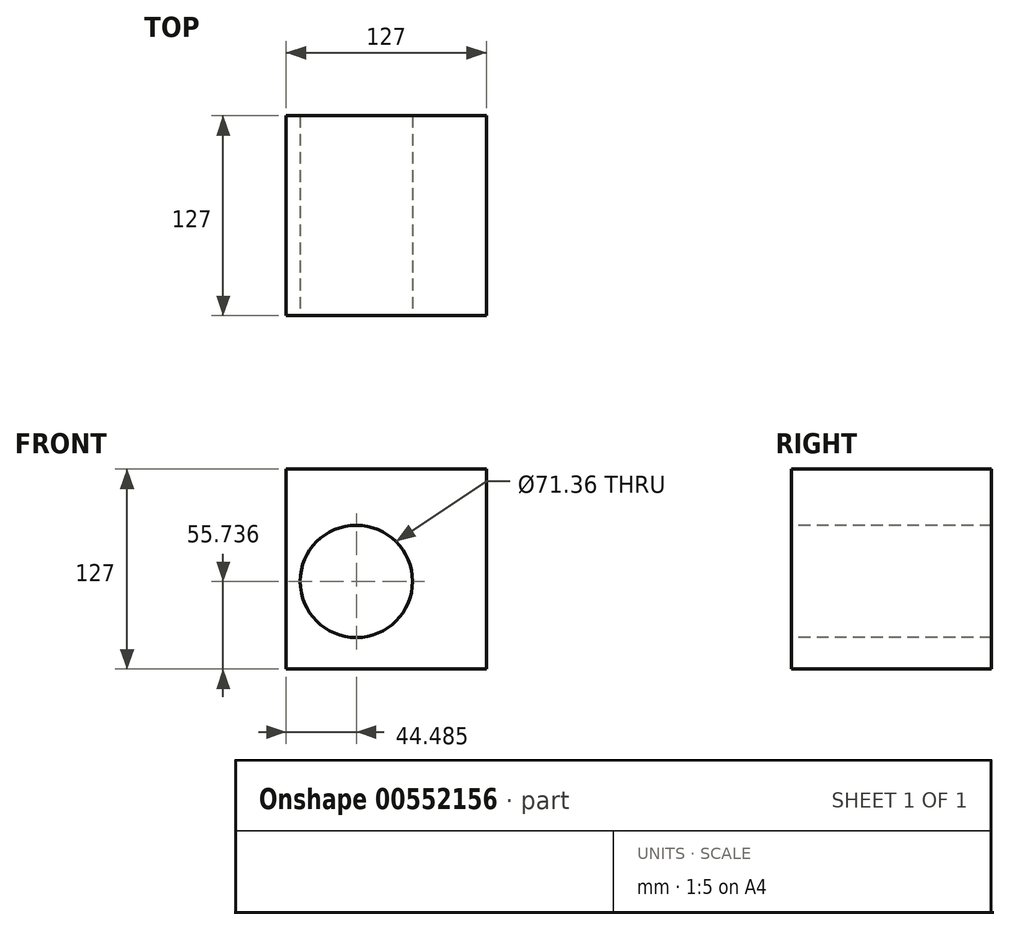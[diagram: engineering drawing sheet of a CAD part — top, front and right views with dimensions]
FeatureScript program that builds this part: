
annotation { "Feature Type Name" : "Feature", "Feature Type Description" : "" }
export const myFeature = defineFeature(function(context is Context, id is Id, definition is map)
    precondition{}
    {
        {
            var Q0;
            Q0=qCreatedBy(makeId("Front.planeOp"),FACE);
            var sketch = newSketch(context, id + "F0", { "sketchPlane" : qUnion([Q0])});
            skLineSegment(sketch, "E0.bottom", {"start": v(-65.6, 78.72) * mm, "end": v(61.4, 78.72) * mm});
            skLineSegment(sketch, "E0.top", {"start": v(-65.6, -48.28) * mm, "end": v(61.4, -48.28) * mm});
            skLineSegment(sketch, "E0.left", {"start": v(-65.6, 78.72) * mm, "end": v(-65.6, -48.28) * mm});
            skLineSegment(sketch, "E0.right", {"start": v(61.4, 78.72) * mm, "end": v(61.4, -48.28) * mm});
            skSolve(sketch);
        }
        {
            var Q0;
            Q0=makeQuery(id+"F0.imprint","IMPRINT",FACE,{"disambiguationData":[TD([[makeQuery(id+"F0.imprint","IMPRINT",EDGE,{"derivedFrom":sQuery(id+"F0.wireOp",EDGE,"E0.bottom")}),-1.0]])]});
            extrude(context, id + "F1", {"entities" : qUnion([Q0]), "depth" : 127 * mm, "offsetDistance" : 25.4 * mm});
        }
        {
            var Q0;
            Q0=makeQuery(id+"F1.opExtrude","CAP_FACE",FACE,{"disambiguationData":[OSD([sQuery(id+"F0.wireOp",EDGE,"E0.bottom"),sQuery(id+"F0.wireOp",EDGE,"E0.top"),sQuery(id+"F0.wireOp",EDGE,"E0.left"),sQuery(id+"F0.wireOp",EDGE,"E0.right")])],"isStart":false});
            var sketch = newSketch(context, id + "F2", { "sketchPlane" : qUnion([Q0])});
            skCircle(sketch, "E1", {"center": v(-21.11, 7.46) * mm, "radius": 35.68 * mm});
            skSolve(sketch);
        }
        {
            var Q0;
            Q0=makeQuery(id+"F2.imprint","IMPRINT",FACE,{"disambiguationData":[TD([[makeQuery(id+"F2.imprint","IMPRINT",EDGE,{"derivedFrom":sQuery(id+"F2.wireOp",EDGE,"E1")}),1.0]])]});
            var Q1;
            Q1=makeQuery(id+"F1.opExtrude","CAP_FACE",FACE,{"disambiguationData":[OSD([sQuery(id+"F0.wireOp",EDGE,"E0.bottom"),sQuery(id+"F0.wireOp",EDGE,"E0.top"),sQuery(id+"F0.wireOp",EDGE,"E0.left"),sQuery(id+"F0.wireOp",EDGE,"E0.right")])],"isStart":true});
            extrude(context, id + "F3", {"entities" : qUnion([Q0]), "operationType" : NewBodyOperationType.REMOVE, "endBound" : BoundingType.UP_TO_SURFACE, "oppositeDirection" : true, "depth" : 12.7 * mm, "endBoundEntityFace" : qUnion([Q1]), "offsetDistance" : 25.4 * mm});
        }
    });
